# Revit family: Cascata Time Power Murale
name_source: partatom
category: Attrezzatura meccanica
units: mm (PartAtom-declared; Revit-internal decimal feet)

## family parameters
Basato su piano di lavoro = No
Condiviso = No
Numero OmniClass = 23.75.00.00
Punto di calcolo locali = No
Quota connettore circolare = Usa diametro
Sempre verticale = Sì
Taglio con vuoti quando caricato = No
Tipo di parte = Normale
Titolo OmniClass = Climate Control (HVAC)

## types (35) — shared parameters
Condensate Drain (cascade) = 40 mm  [stored 0.131234 ft]
Date of publishing = 30/10/2020
Design country = Italy
Equilibratore_DX = Sì
Equilibratore_SX = Sì
Gas Inlet Diameter (cascade) = 48 mm  [stored 0.15748 ft]
Manufacturer country = Italy
Manufacturer name = Italtherm S.p.A.
Material main = Metal
Material secondary = Plastic
On_FumiDX_Off_FumiSX = Sì
Product family = Heating
Product group = Thermal unit
Scambiatore_DX = Sì
Scambiatore_SX = Sì
URL = https://www.italtherm.it
URL ENG = https://en.italtherm.it
Vis.Equil.dx = Sì
Vis.Equil.sx = Sì
Vis.FumiDX = Sì
Vis.FumiSX = No
Vis.Scamb.dx = Sì
Vis.Scamb.sx = Sì
zero-valued in all types: Edition number, Prospetto di default

## per-type parameters (varying)
| type | Caldaia_0 | Caldaia_1 | Caldaia_2 | Caldaia_3 | Diam_flange_equilib | Distanza_kit_INAIL | Flue outlet (cascade) | Hydronic Return Diameter (cascade) | Hydronic Supply Diameter (cascade) | Maximum heating heat input | NascTubo | NumeroCaldaie | Numero_Caldaie | Qn_MAX | Sottr | Vis.scarico3 | Vis.scarico4 | Visibilità_caldaia_2 | Visibilità_caldaia_3 |
| 190 kW_4 Caldaie | Time Power : Time Power 50 K | Time Power : Time Power 50 K | Time Power : Time Power 50 K | Time Power : Time Power 50 K | 185 mm  [stored 0.606955 ft] | 2800 mm  [stored 9.18635 ft] | 160 mm  [stored 0.524934 ft] | 185 mm  [stored 0.606955 ft] | 185 mm  [stored 0.606955 ft] | 190 kW | 5100 mm  [stored 16.7323 ft] | 4 | 4 | 190 kW | 3100 mm  [stored 10.1706 ft] | Sì | Sì | Sì | Sì |
| 206 kW_4 Caldaie | Time Power : Time Power 50 K | Time Power : Time Power 50 K | Time Power : Time Power 50 K | Time Power : Time power 70 K | 185 mm  [stored 0.606955 ft] | 2800 mm  [stored 9.18635 ft] | 160 mm  [stored 0.524934 ft] | 185 mm  [stored 0.606955 ft] | 185 mm  [stored 0.606955 ft] | 206 kW | 5100 mm  [stored 16.7323 ft] | 4 | 4 | 206 kW | 3100 mm  [stored 10.1706 ft] | Sì | Sì | Sì | Sì |
| 221 kW_4 Caldaie | Time Power : Time Power 50 K | Time Power : Time Power 50 K | Time Power : Time power 70 K | Time Power : Time power 70 K | 185 mm  [stored 0.606955 ft] | 2800 mm  [stored 9.18635 ft] | 160 mm  [stored 0.524934 ft] | 185 mm  [stored 0.606955 ft] | 185 mm  [stored 0.606955 ft] | 221 kW | 5100 mm  [stored 16.7323 ft] | 4 | 4 | 221 kW | 3100 mm  [stored 10.1706 ft] | Sì | Sì | Sì | Sì |
| 237 kW_4 Caldaie | Time Power : Time Power 50 K | Time Power : Time power 70 K | Time Power : Time power 70 K | Time Power : Time power 70 K | 185 mm  [stored 0.606955 ft] | 2800 mm  [stored 9.18635 ft] | 160 mm  [stored 0.524934 ft] | 185 mm  [stored 0.606955 ft] | 185 mm  [stored 0.606955 ft] | 237 kW | 5100 mm  [stored 16.7323 ft] | 4 | 4 | 237 kW | 3100 mm  [stored 10.1706 ft] | Sì | Sì | Sì | Sì |
| 252 kW_4 Caldaie | Time Power : Time power 70 K | Time Power : Time power 70 K | Time Power : Time power 70 K | Time Power : Time power 70 K | 185 mm  [stored 0.606955 ft] | 2800 mm  [stored 9.18635 ft] | 160 mm  [stored 0.524934 ft] | 185 mm  [stored 0.606955 ft] | 185 mm  [stored 0.606955 ft] | 252 kW | 5100 mm  [stored 16.7323 ft] | 4 | 4 | 252 kW | 3100 mm  [stored 10.1706 ft] | Sì | Sì | Sì | Sì |
| 340 kW_4 Caldaie | Time Power : Time Power 90 K | Time Power : Time Power 90 K | Time Power : Time Power 90 K | Time Power : Time Power 90 K | 210 mm  [stored 0.688976 ft] | 2800 mm  [stored 9.18635 ft] | 200 mm  [stored 0.656168 ft] | 210 mm  [stored 0.688976 ft] | 210 mm  [stored 0.688976 ft] | 340 kW | 5100 mm  [stored 16.7323 ft] | 4 | 4 | 340 kW | 3100 mm  [stored 10.1706 ft] | Sì | Sì | Sì | Sì |
| 363 kW_4 Caldaie | Time Power : Time Power 90 K | Time Power : Time Power 90 K | Time Power : Time Power 90 K | Time Power : Time Power 115 K | 210 mm  [stored 0.688976 ft] | 2800 mm  [stored 9.18635 ft] | 200 mm  [stored 0.656168 ft] | 210 mm  [stored 0.688976 ft] | 210 mm  [stored 0.688976 ft] | 363 kW | 5100 mm  [stored 16.7323 ft] | 4 | 4 | 363 kW | 3100 mm  [stored 10.1706 ft] | Sì | Sì | Sì | Sì |
| 386 kW_4 Caldaie | Time Power : Time Power 90 K | Time Power : Time Power 90 K | Time Power : Time Power 115 K | Time Power : Time Power 115 K | 210 mm  [stored 0.688976 ft] | 2800 mm  [stored 9.18635 ft] | 200 mm  [stored 0.656168 ft] | 210 mm  [stored 0.688976 ft] | 210 mm  [stored 0.688976 ft] | 386 kW | 5100 mm  [stored 16.7323 ft] | 4 | 4 | 386 kW | 3100 mm  [stored 10.1706 ft] | Sì | Sì | Sì | Sì |
| 405 kW_4 Caldaie | Time Power : Time Power 160 K | Time Power : Time Power 90 K | Time Power : Time Power 90 K | Time Power : Time Power 90 K | 210 mm  [stored 0.688976 ft] | 2800 mm  [stored 9.18635 ft] | 200 mm  [stored 0.656168 ft] | 210 mm  [stored 0.688976 ft] | 210 mm  [stored 0.688976 ft] | 405 kW | 5100 mm  [stored 16.7323 ft] | 4 | 4 | 405 kW | 3100 mm  [stored 10.1706 ft] | Sì | Sì | Sì | Sì |
| 409 kW_4 Caldaie | Time Power : Time Power 115 K | Time Power : Time Power 115 K | Time Power : Time Power 115 K | Time Power : Time Power 90 K | 210 mm  [stored 0.688976 ft] | 2800 mm  [stored 9.18635 ft] | 200 mm  [stored 0.656168 ft] | 210 mm  [stored 0.688976 ft] | 210 mm  [stored 0.688976 ft] | 409 kW | 5100 mm  [stored 16.7323 ft] | 4 | 4 | 409 kW | 3100 mm  [stored 10.1706 ft] | Sì | Sì | Sì | Sì |
| 428 kW_4 Caldaie | Time Power : Time Power 160 K | Time Power : Time Power 115 K | Time Power : Time Power 90 K | Time Power : Time Power 90 K | 210 mm  [stored 0.688976 ft] | 2800 mm  [stored 9.18635 ft] | 200 mm  [stored 0.656168 ft] | 210 mm  [stored 0.688976 ft] | 210 mm  [stored 0.688976 ft] | 428 kW | 5100 mm  [stored 16.7323 ft] | 4 | 4 | 428 kW | 3100 mm  [stored 10.1706 ft] | Sì | Sì | Sì | Sì |
| 432 kW_4 Caldaie | Time Power : Time Power 115 K | Time Power : Time Power 115 K | Time Power : Time Power 115 K | Time Power : Time Power 115 K | 210 mm  [stored 0.688976 ft] | 2800 mm  [stored 9.18635 ft] | 200 mm  [stored 0.656168 ft] | 210 mm  [stored 0.688976 ft] | 210 mm  [stored 0.688976 ft] | 432 kW | 5100 mm  [stored 16.7323 ft] | 4 | 4 | 432 kW | 3100 mm  [stored 10.1706 ft] | Sì | Sì | Sì | Sì |
| 143 kW_3 Caldaie | Time Power : Time Power 50 K | Time Power : Time Power 50 K | Time Power : Time Power 50 K | Time Power : Nessuna | 185 mm  [stored 0.606955 ft] | 2100 mm | 125 mm  [stored 0.410105 ft] | 185 mm  [stored 0.606955 ft] | 185 mm  [stored 0.606955 ft] | 143 kW | 4400 mm | 3 | 3 | 143 kW | 2400 mm | Sì | No | Sì | No |
| 158 kW_3 Caldaie | Time Power : Time Power 50 K | Time Power : Time Power 50 K | Time Power : Time power 70 K | Time Power : Nessuna | 185 mm  [stored 0.606955 ft] | 2100 mm | 125 mm  [stored 0.410105 ft] | 185 mm  [stored 0.606955 ft] | 185 mm  [stored 0.606955 ft] | 158 kW | 4400 mm | 3 | 3 | 158 kW | 2400 mm | Sì | No | Sì | No |
| 174 kW_3 Caldaie | Time Power : Time Power 50 K | Time Power : Time power 70 K | Time Power : Time power 70 K | Time Power : Nessuna | 185 mm  [stored 0.606955 ft] | 2100 mm | 160 mm  [stored 0.524934 ft] | 185 mm  [stored 0.606955 ft] | 185 mm  [stored 0.606955 ft] | 174 kW | 4400 mm | 3 | 3 | 174 kW | 2400 mm | Sì | No | Sì | No |
| 189 kW_3 Caldaie | Time Power : Time power 70 K | Time Power : Time power 70 K | Time Power : Time power 70 K | Time Power : Nessuna | 185 mm  [stored 0.606955 ft] | 2100 mm | 160 mm  [stored 0.524934 ft] | 185 mm  [stored 0.606955 ft] | 185 mm  [stored 0.606955 ft] | 189 kW | 4400 mm | 3 | 3 | 189 kW | 2400 mm | Sì | No | Sì | No |
| 255 kW_3 Caldaie | Time Power : Time Power 90 K | Time Power : Time Power 90 K | Time Power : Time Power 90 K | Time Power : Nessuna | 185 mm  [stored 0.606955 ft] | 2100 mm | 160 mm  [stored 0.524934 ft] | 185 mm  [stored 0.606955 ft] | 185 mm  [stored 0.606955 ft] | 255 kW | 4400 mm | 3 | 3 | 255 kW | 2400 mm | Sì | No | Sì | No |
| 278 kW_3 Caldaie | Time Power : Time Power 90 K | Time Power : Time Power 90 K | Time Power : Time Power 115 K | Time Power : Nessuna | 185 mm  [stored 0.606955 ft] | 2100 mm | 200 mm  [stored 0.656168 ft] | 185 mm  [stored 0.606955 ft] | 185 mm  [stored 0.606955 ft] | 278 kW | 4400 mm | 3 | 3 | 278 kW | 2400 mm | Sì | No | Sì | No |
| 301 kW_3 Caldaie | Time Power : Time Power 90 K | Time Power : Time Power 115 K | Time Power : Time Power 115 K | Time Power : Nessuna | 210 mm  [stored 0.688976 ft] | 2100 mm | 200 mm  [stored 0.656168 ft] | 210 mm  [stored 0.688976 ft] | 210 mm  [stored 0.688976 ft] | 301 kW | 4400 mm | 3 | 3 | 301 kW | 2400 mm | Sì | No | Sì | No |
| 320 kW_3 Caldaie | Time Power : Time Power 160 K | Time Power : Time Power 90 K | Time Power : Time Power 90 K | Time Power : Nessuna | 210 mm  [stored 0.688976 ft] | 2100 mm | 200 mm  [stored 0.656168 ft] | 210 mm  [stored 0.688976 ft] | 210 mm  [stored 0.688976 ft] | 320 kW | 4400 mm | 3 | 3 | 320 kW | 2400 mm | Sì | No | Sì | No |
| 324 kW_3 Caldaie | Time Power : Time Power 115 K | Time Power : Time Power 115 K | Time Power : Time Power 115 K | Time Power : Nessuna | 210 mm  [stored 0.688976 ft] | 2100 mm | 200 mm  [stored 0.656168 ft] | 210 mm  [stored 0.688976 ft] | 210 mm  [stored 0.688976 ft] | 324 kW | 4400 mm | 3 | 3 | 324 kW | 2400 mm | Sì | No | Sì | No |
| 343 kW_3 Caldaie | Time Power : Time Power 160 K | Time Power : Time Power 115 K | Time Power : Time Power 90 K | Time Power : Nessuna | 210 mm  [stored 0.688976 ft] | 2100 mm | 200 mm  [stored 0.656168 ft] | 210 mm  [stored 0.688976 ft] | 210 mm  [stored 0.688976 ft] | 343 kW | 4400 mm | 3 | 3 | 343 kW | 2400 mm | Sì | No | Sì | No |
| 366 kW_3 Caldaie | Time Power : Time Power 160 K | Time Power : Time Power 115 K | Time Power : Time Power 115 K | Time Power : Nessuna | 210 mm  [stored 0.688976 ft] | 2100 mm | 200 mm  [stored 0.656168 ft] | 210 mm  [stored 0.688976 ft] | 210 mm  [stored 0.688976 ft] | 366 kW | 4400 mm | 3 | 3 | 366 kW | 2400 mm | Sì | No | Sì | No |
| 385 kW_3 Caldaie | Time Power : Time Power 160 K | Time Power : Time Power 160 K | Time Power : Time Power 90 K | Time Power : Nessuna | 210 mm  [stored 0.688976 ft] | 2100 mm | 200 mm  [stored 0.656168 ft] | 210 mm  [stored 0.688976 ft] | 210 mm  [stored 0.688976 ft] | 385 kW | 4400 mm | 3 | 3 | 385 kW | 2400 mm | Sì | No | Sì | No |
| 408 kW_3 Caldaie | Time Power : Time Power 160 K | Time Power : Time Power 160 K | Time Power : Time Power 115 K | Time Power : Nessuna | 210 mm  [stored 0.688976 ft] | 2100 mm | 200 mm  [stored 0.656168 ft] | 210 mm  [stored 0.688976 ft] | 210 mm  [stored 0.688976 ft] | 408 kW | 4400 mm | 3 | 3 | 408 kW | 2400 mm | Sì | No | Sì | No |
| 450 kW_3 Caldaie | Time Power : Time Power 160 K | Time Power : Time Power 160 K | Time Power : Time Power 160 K | Time Power : Nessuna | 210 mm  [stored 0.688976 ft] | 2100 mm | 200 mm  [stored 0.656168 ft] | 210 mm  [stored 0.688976 ft] | 210 mm  [stored 0.688976 ft] | 450 kW | 4400 mm | 3 | 3 | 450 kW | 2400 mm | Sì | No | Sì | No |
| 095 kW_2 Caldaie | Time Power : Time Power 50 K | Time Power : Time Power 50 K | Time Power : Nessuna | Time Power : Nessuna | 185 mm  [stored 0.606955 ft] | 1400 mm  [stored 4.59318 ft] | 125 mm  [stored 0.410105 ft] | 185 mm  [stored 0.606955 ft] | 185 mm  [stored 0.606955 ft] | 95 kW | 3700 mm  [stored 12.1391 ft] | 2 | 2 | 95 kW | 1700 mm  [stored 5.57743 ft] | No | No | No | No |
| 111 kW_2 Caldaie | Time Power : Time Power 50 K | Time Power : Time power 70 K | Time Power : Nessuna | Time Power : Nessuna | 185 mm  [stored 0.606955 ft] | 1400 mm  [stored 4.59318 ft] | 125 mm  [stored 0.410105 ft] | 185 mm  [stored 0.606955 ft] | 185 mm  [stored 0.606955 ft] | 111 kW | 3700 mm  [stored 12.1391 ft] | 2 | 2 | 111 kW | 1700 mm  [stored 5.57743 ft] | No | No | No | No |
| 126 kW_2 Caldaie | Time Power : Time power 70 K | Time Power : Time power 70 K | Time Power : Nessuna | Time Power : Nessuna | 185 mm  [stored 0.606955 ft] | 1400 mm  [stored 4.59318 ft] | 125 mm  [stored 0.410105 ft] | 185 mm  [stored 0.606955 ft] | 185 mm  [stored 0.606955 ft] | 126 kW | 3700 mm  [stored 12.1391 ft] | 2 | 2 | 126 kW | 1700 mm  [stored 5.57743 ft] | No | No | No | No |
| 170 kW_2 Caldaie | Time Power : Time Power 90 K | Time Power : Time Power 90 K | Time Power : Nessuna | Time Power : Nessuna | 185 mm  [stored 0.606955 ft] | 1400 mm  [stored 4.59318 ft] | 160 mm  [stored 0.524934 ft] | 185 mm  [stored 0.606955 ft] | 185 mm  [stored 0.606955 ft] | 170 kW | 3700 mm  [stored 12.1391 ft] | 2 | 2 | 170 kW | 1700 mm  [stored 5.57743 ft] | No | No | No | No |
| 193 kW_2 Caldaie | Time Power : Time Power 90 K | Time Power : Time Power 115 K | Time Power : Nessuna | Time Power : Nessuna | 185 mm  [stored 0.606955 ft] | 1400 mm  [stored 4.59318 ft] | 160 mm  [stored 0.524934 ft] | 185 mm  [stored 0.606955 ft] | 185 mm  [stored 0.606955 ft] | 193 kW | 3700 mm  [stored 12.1391 ft] | 2 | 2 | 193 kW | 1700 mm  [stored 5.57743 ft] | No | No | No | No |
| 216 kW_2 Caldaie | Time Power : Time Power 115 K | Time Power : Time Power 115 K | Time Power : Nessuna | Time Power : Nessuna | 185 mm  [stored 0.606955 ft] | 1400 mm  [stored 4.59318 ft] | 160 mm  [stored 0.524934 ft] | 185 mm  [stored 0.606955 ft] | 185 mm  [stored 0.606955 ft] | 216 kW | 3700 mm  [stored 12.1391 ft] | 2 | 2 | 216 kW | 1700 mm  [stored 5.57743 ft] | No | No | No | No |
| 235 kW_2 Caldaie | Time Power : Time Power 160 K | Time Power : Time Power 90 K | Time Power : Nessuna | Time Power : Nessuna | 185 mm  [stored 0.606955 ft] | 1400 mm  [stored 4.59318 ft] | 160 mm  [stored 0.524934 ft] | 185 mm  [stored 0.606955 ft] | 185 mm  [stored 0.606955 ft] | 235 kW | 3700 mm  [stored 12.1391 ft] | 2 | 2 | 235 kW | 1700 mm  [stored 5.57743 ft] | No | No | No | No |
| 258 kW_2 Caldaie | Time Power : Time Power 160 K | Time Power : Time Power 115 K | Time Power : Nessuna | Time Power : Nessuna | 185 mm  [stored 0.606955 ft] | 1400 mm  [stored 4.59318 ft] | 160 mm  [stored 0.524934 ft] | 185 mm  [stored 0.606955 ft] | 185 mm  [stored 0.606955 ft] | 258 kW | 3700 mm  [stored 12.1391 ft] | 2 | 2 | 258 kW | 1700 mm  [stored 5.57743 ft] | No | No | No | No |
| 300 kW_2 Caldaie | Time Power : Time Power 160 K | Time Power : Time Power 160 K | Time Power : Nessuna | Time Power : Nessuna | 210 mm  [stored 0.688976 ft] | 1400 mm  [stored 4.59318 ft] | 200 mm  [stored 0.656168 ft] | 210 mm  [stored 0.688976 ft] | 210 mm  [stored 0.688976 ft] | 300 kW | 3700 mm  [stored 12.1391 ft] | 2 | 2 | 300 kW | 1700 mm  [stored 5.57743 ft] | No | No | No | No |

note: [stored X ft] marks values corroborated as IEEE doubles in the binary element streams (Revit-internal decimal feet)
